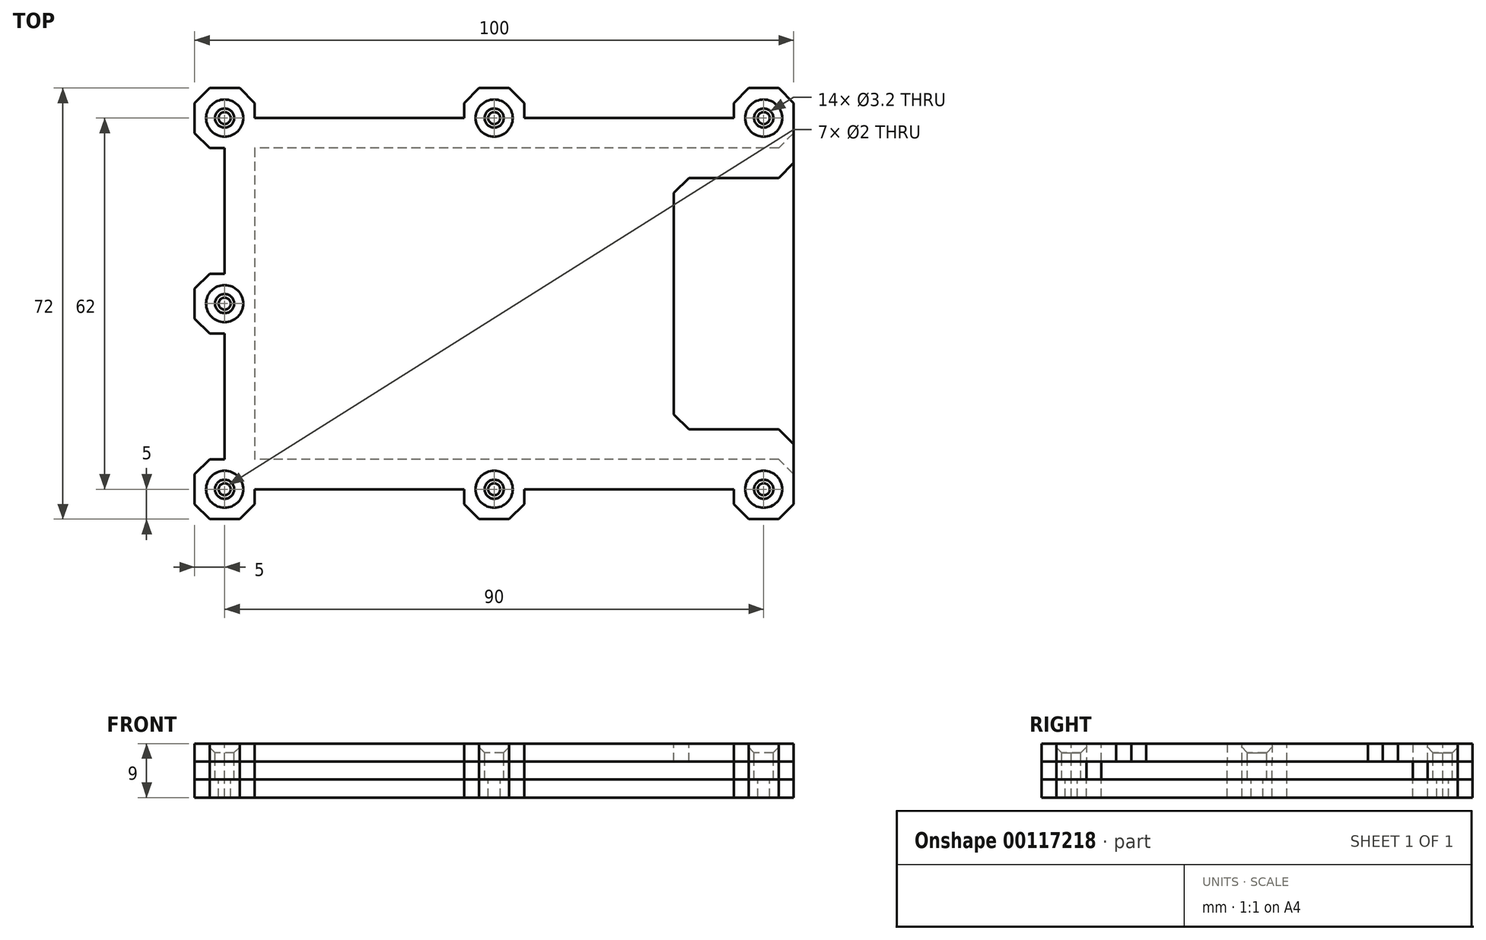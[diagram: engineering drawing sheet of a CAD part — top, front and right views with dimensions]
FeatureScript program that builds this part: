
annotation { "Feature Type Name" : "Feature", "Feature Type Description" : "" }
export const myFeature = defineFeature(function(context is Context, id is Id, definition is map)
    precondition{}
    {
        {
            var Q0;
            Q0=qCreatedBy(makeId("Top.planeOp"),FACE);
            var sketch = newSketch(context, id + "F0", { "sketchPlane" : qUnion([Q0])});
            skLineSegment(sketch, "E0.bottom", {"start": v(45, -26) * mm, "end": v(-37, -26) * mm});
            skLineSegment(sketch, "E0.top", {"start": v(45, 26) * mm, "end": v(-37, 26) * mm});
            skLineSegment(sketch, "E0.left", {"start": v(45, -36) * mm, "end": v(45, 36) * mm});
            skLineSegment(sketch, "E0.right", {"start": v(-45, -18) * mm, "end": v(-45, 18) * mm});
            skPoint(sketch, "E0.middle", {"position": v(0, 0) * mm});
            skPoint(sketch, "E1.visualSharp", {"position": v(-45, 26) * mm});
            skArc(sketch, "E1.filletArc", {"start": v(-37, 26) * mm, "mid": v(-42.66, 23.66) * mm, "end": v(-45, 18) * mm});
            skPoint(sketch, "E2.visualSharp", {"position": v(-45, -26) * mm});
            skArc(sketch, "E2.filletArc", {"start": v(-45, -18) * mm, "mid": v(-42.66, -23.66) * mm, "end": v(-37, -26) * mm});
            skLineSegment(sketch, "E3.bottom", {"start": v(45, -36) * mm, "end": v(35, -36) * mm});
            skLineSegment(sketch, "E3.right", {"start": v(-55, -36) * mm, "end": v(-55, -26) * mm});
            skLineSegment(sketch, "E4.top", {"start": v(-45, 31) * mm, "end": v(-10, 31) * mm});
            skLineSegment(sketch, "E4.left", {"start": v(-45, 36) * mm, "end": v(-45, 31) * mm});
            skLineSegment(sketch, "E4.right", {"start": v(-10, 36) * mm, "end": v(-10, 31) * mm});
            skLineSegment(sketch, "E5.top", {"start": v(0, 31) * mm, "end": v(35, 31) * mm});
            skLineSegment(sketch, "E5.left", {"start": v(0, 36) * mm, "end": v(0, 31) * mm});
            skLineSegment(sketch, "E5.right", {"start": v(35, 36) * mm, "end": v(35, 31) * mm});
            skLineSegment(sketch, "E6.bottom", {"start": v(0, -31) * mm, "end": v(35, -31) * mm});
            skLineSegment(sketch, "E6.left", {"start": v(0, -31) * mm, "end": v(0, -36) * mm});
            skLineSegment(sketch, "E6.right", {"start": v(35, -31) * mm, "end": v(35, -36) * mm});
            skLineSegment(sketch, "E7.bottom", {"start": v(-45, -31) * mm, "end": v(-10, -31) * mm});
            skLineSegment(sketch, "E7.left", {"start": v(-45, -31) * mm, "end": v(-45, -36) * mm});
            skLineSegment(sketch, "E7.right", {"start": v(-10, -31) * mm, "end": v(-10, -36) * mm});
            skLineSegment(sketch, "E8.trimOffspring", {"start": v(45, 36) * mm, "end": v(35, 36) * mm});
            skPoint(sketch, "E3.left.end.orphan", {"position": v(55, 36) * mm});
            skPoint(sketch, "E9.orphan", {"position": v(55, -36) * mm});
            skLineSegment(sketch, "E10.trimOffspring", {"start": v(-45, 36) * mm, "end": v(-55, 36) * mm});
            skLineSegment(sketch, "E11.trimOffspring", {"start": v(0, 36) * mm, "end": v(-10, 36) * mm});
            skLineSegment(sketch, "E12.trimOffspring", {"start": v(0, -36) * mm, "end": v(-10, -36) * mm});
            skLineSegment(sketch, "E13.trimOffspring", {"start": v(-45, -36) * mm, "end": v(-55, -36) * mm});
            skLineSegment(sketch, "E14.bottom", {"start": v(-55, 26) * mm, "end": v(-50, 26) * mm});
            skLineSegment(sketch, "E14.top", {"start": v(-55, 5) * mm, "end": v(-50, 5) * mm});
            skLineSegment(sketch, "E14.right", {"start": v(-50, 26) * mm, "end": v(-50, 5) * mm});
            skLineSegment(sketch, "E15.bottom", {"start": v(-55, -5) * mm, "end": v(-50, -5) * mm});
            skLineSegment(sketch, "E15.top", {"start": v(-55, -26) * mm, "end": v(-50, -26) * mm});
            skLineSegment(sketch, "E15.right", {"start": v(-50, -5) * mm, "end": v(-50, -26) * mm});
            skLineSegment(sketch, "E16.trimOffspring", {"start": v(-55, 26) * mm, "end": v(-55, 36) * mm});
            skLineSegment(sketch, "E17.trimOffspring", {"start": v(-55, -5) * mm, "end": v(-55, 5) * mm});
            skLineSegment(sketch, "E18", {"start": v(-45, 36) * mm, "end": v(-55, 26) * mm, "construction": true});
            skLineSegment(sketch, "E19", {"start": v(-10, 31) * mm, "end": v(0, 31) * mm, "construction": true});
            skLineSegment(sketch, "E20", {"start": v(35, 36) * mm, "end": v(45, 26) * mm, "construction": true});
            skLineSegment(sketch, "E21", {"start": v(45, -26) * mm, "end": v(35, -36) * mm, "construction": true});
            skLineSegment(sketch, "E22", {"start": v(0, -31) * mm, "end": v(-10, -31) * mm, "construction": true});
            skLineSegment(sketch, "E23", {"start": v(-45, -36) * mm, "end": v(-55, -26) * mm, "construction": true});
            skCircle(sketch, "E24", {"center": v(-50, 31) * mm, "radius": 1.6 * mm});
            skCircle(sketch, "E25", {"center": v(-5, 31) * mm, "radius": 1.6 * mm});
            skCircle(sketch, "E26", {"center": v(40, 31) * mm, "radius": 1.6 * mm});
            skCircle(sketch, "E27", {"center": v(40, -31) * mm, "radius": 1.6 * mm});
            skCircle(sketch, "E28", {"center": v(-5, -31) * mm, "radius": 1.6 * mm});
            skCircle(sketch, "E29", {"center": v(-50, -31) * mm, "radius": 1.6 * mm});
            skLineSegment(sketch, "E30", {"start": v(-50, 5) * mm, "end": v(-50, -5) * mm, "construction": true});
            skCircle(sketch, "E31", {"center": v(-50, 0) * mm, "radius": 1.6 * mm});
            skSolve(sketch);
        }
        {
            var Q0;
            {var subQ1=sQuery(id+"F0.wireOp",EDGE,"E0.bottom");Q0=makeQuery(id+"F0.imprint","IMPRINT",FACE,{"disambiguationData":[TD([[makeQuery(id+"F0.imprint","IMPRINT",EDGE,{"derivedFrom":subQ1}),-1.0]])]});}
            var Q1;
            {var subQ3=sQuery(id+"F0.wireOp",EDGE,"E0.bottom");Q1=makeQuery(id+"F0.imprint","IMPRINT",FACE,{"disambiguationData":[TD([[makeQuery(id+"F0.imprint","IMPRINT",EDGE,{"derivedFrom":subQ3}),1.0]])]});}
            extrude(context, id + "F1", {"entities" : qUnion([Q0, Q1]), "oppositeDirection" : true, "depth" : 3 * mm});
        }
        {
            var Q0;
            Q0=makeQuery(id+"F1.opExtrude","SWEPT_EDGE",EDGE,{"disambiguationData":[OSD([sQuery(id+"F0.wireOp",EDGE,"E0.left"),sQuery(id+"F0.wireOp",EDGE,"E3.bottom")])]});
            var Q1;
            Q1=makeQuery(id+"F1.opExtrude","SWEPT_EDGE",EDGE,{"disambiguationData":[OSD([sQuery(id+"F0.wireOp",EDGE,"E3.bottom"),sQuery(id+"F0.wireOp",EDGE,"E6.right")])]});
            var Q2;
            Q2=makeQuery(id+"F1.opExtrude","SWEPT_EDGE",EDGE,{"disambiguationData":[OSD([sQuery(id+"F0.wireOp",EDGE,"E6.left"),sQuery(id+"F0.wireOp",EDGE,"E12.trimOffspring")])]});
            var Q3;
            Q3=makeQuery(id+"F1.opExtrude","SWEPT_EDGE",EDGE,{"disambiguationData":[OSD([sQuery(id+"F0.wireOp",EDGE,"E7.right"),sQuery(id+"F0.wireOp",EDGE,"E12.trimOffspring")])]});
            var Q4;
            Q4=makeQuery(id+"F1.opExtrude","SWEPT_EDGE",EDGE,{"disambiguationData":[OSD([sQuery(id+"F0.wireOp",EDGE,"E7.left"),sQuery(id+"F0.wireOp",EDGE,"E13.trimOffspring")])]});
            var Q5;
            Q5=makeQuery(id+"F1.opExtrude","SWEPT_EDGE",EDGE,{"disambiguationData":[OSD([sQuery(id+"F0.wireOp",EDGE,"E3.right"),sQuery(id+"F0.wireOp",EDGE,"E13.trimOffspring")])]});
            var Q6;
            Q6=makeQuery(id+"F1.opExtrude","SWEPT_EDGE",EDGE,{"disambiguationData":[OSD([sQuery(id+"F0.wireOp",EDGE,"E15.bottom"),sQuery(id+"F0.wireOp",EDGE,"E17.trimOffspring")])]});
            var Q7;
            Q7=makeQuery(id+"F1.opExtrude","SWEPT_EDGE",EDGE,{"disambiguationData":[OSD([sQuery(id+"F0.wireOp",EDGE,"E14.bottom"),sQuery(id+"F0.wireOp",EDGE,"E16.trimOffspring")])]});
            var Q8;
            Q8=makeQuery(id+"F1.opExtrude","SWEPT_EDGE",EDGE,{"disambiguationData":[OSD([sQuery(id+"F0.wireOp",EDGE,"E3.right"),sQuery(id+"F0.wireOp",EDGE,"E15.top")])]});
            var Q9;
            Q9=makeQuery(id+"F1.opExtrude","SWEPT_EDGE",EDGE,{"disambiguationData":[OSD([sQuery(id+"F0.wireOp",EDGE,"E14.top"),sQuery(id+"F0.wireOp",EDGE,"E17.trimOffspring")])]});
            var Q10;
            Q10=makeQuery(id+"F1.opExtrude","SWEPT_EDGE",EDGE,{"disambiguationData":[OSD([sQuery(id+"F0.wireOp",EDGE,"E10.trimOffspring"),sQuery(id+"F0.wireOp",EDGE,"E16.trimOffspring")])]});
            var Q11;
            Q11=makeQuery(id+"F1.opExtrude","SWEPT_EDGE",EDGE,{"disambiguationData":[OSD([sQuery(id+"F0.wireOp",EDGE,"E4.left"),sQuery(id+"F0.wireOp",EDGE,"E10.trimOffspring")])]});
            var Q12;
            Q12=makeQuery(id+"F1.opExtrude","SWEPT_EDGE",EDGE,{"disambiguationData":[OSD([sQuery(id+"F0.wireOp",EDGE,"E4.right"),sQuery(id+"F0.wireOp",EDGE,"E11.trimOffspring")])]});
            var Q13;
            Q13=makeQuery(id+"F1.opExtrude","SWEPT_EDGE",EDGE,{"disambiguationData":[OSD([sQuery(id+"F0.wireOp",EDGE,"E5.left"),sQuery(id+"F0.wireOp",EDGE,"E11.trimOffspring")])]});
            var Q14;
            Q14=makeQuery(id+"F1.opExtrude","SWEPT_EDGE",EDGE,{"disambiguationData":[OSD([sQuery(id+"F0.wireOp",EDGE,"E5.right"),sQuery(id+"F0.wireOp",EDGE,"E8.trimOffspring")])]});
            var Q15;
            Q15=makeQuery(id+"F1.opExtrude","SWEPT_EDGE",EDGE,{"disambiguationData":[OSD([sQuery(id+"F0.wireOp",EDGE,"E0.left"),sQuery(id+"F0.wireOp",EDGE,"E8.trimOffspring")])]});
            chamfer(context, id + "F2", {"entities" : qUnion([Q0, Q1, Q2, Q3, Q4, Q5, Q6, Q7, Q8, Q9, Q10, Q11, Q12, Q13, Q14, Q15]), "width" : 2.5 * mm, "tangentPropagation" : true});
        }
        {
            var Q0;
            Q0=makeQuery(id+"F1.opExtrude","CAP_FACE",FACE,{"disambiguationData":[OSD([sQuery(id+"F0.wireOp",EDGE,"E0.left"),sQuery(id+"F0.wireOp",EDGE,"E3.bottom"),sQuery(id+"F0.wireOp",EDGE,"E3.right"),sQuery(id+"F0.wireOp",EDGE,"E4.top"),sQuery(id+"F0.wireOp",EDGE,"E4.left"),sQuery(id+"F0.wireOp",EDGE,"E4.right"),sQuery(id+"F0.wireOp",EDGE,"E5.top"),sQuery(id+"F0.wireOp",EDGE,"E5.left"),sQuery(id+"F0.wireOp",EDGE,"E5.right"),sQuery(id+"F0.wireOp",EDGE,"E6.bottom"),sQuery(id+"F0.wireOp",EDGE,"E6.left"),sQuery(id+"F0.wireOp",EDGE,"E6.right"),sQuery(id+"F0.wireOp",EDGE,"E7.bottom"),sQuery(id+"F0.wireOp",EDGE,"E7.left"),sQuery(id+"F0.wireOp",EDGE,"E7.right"),sQuery(id+"F0.wireOp",EDGE,"E8.trimOffspring"),sQuery(id+"F0.wireOp",EDGE,"E10.trimOffspring"),sQuery(id+"F0.wireOp",EDGE,"E11.trimOffspring"),sQuery(id+"F0.wireOp",EDGE,"E12.trimOffspring"),sQuery(id+"F0.wireOp",EDGE,"E13.trimOffspring"),sQuery(id+"F0.wireOp",EDGE,"E14.bottom"),sQuery(id+"F0.wireOp",EDGE,"E14.top"),sQuery(id+"F0.wireOp",EDGE,"E14.right"),sQuery(id+"F0.wireOp",EDGE,"E15.bottom"),sQuery(id+"F0.wireOp",EDGE,"E15.top"),sQuery(id+"F0.wireOp",EDGE,"E15.right"),sQuery(id+"F0.wireOp",EDGE,"E16.trimOffspring"),sQuery(id+"F0.wireOp",EDGE,"E17.trimOffspring"),sQuery(id+"F0.wireOp",EDGE,"E24"),sQuery(id+"F0.wireOp",EDGE,"E25"),sQuery(id+"F0.wireOp",EDGE,"E26"),sQuery(id+"F0.wireOp",EDGE,"E27"),sQuery(id+"F0.wireOp",EDGE,"E28"),sQuery(id+"F0.wireOp",EDGE,"E29"),sQuery(id+"F0.wireOp",EDGE,"E31")])],"isStart":false});
            var sketch = newSketch(context, id + "F3", { "sketchPlane" : qUnion([Q0])});
            skLineSegment(sketch, "E32", {"start": v(42.5, -36) * mm, "end": v(37.5, -36) * mm});
            skLineSegment(sketch, "E33", {"start": v(42.5, -36) * mm, "end": v(45, -33.5) * mm});
            skLineSegment(sketch, "E34", {"start": v(45, 33.5) * mm, "end": v(45, 26) * mm});
            skLineSegment(sketch, "E35", {"start": v(45, 33.5) * mm, "end": v(42.5, 36) * mm});
            skLineSegment(sketch, "E36", {"start": v(42.5, 36) * mm, "end": v(37.5, 36) * mm});
            skLineSegment(sketch, "E37", {"start": v(37.5, 36) * mm, "end": v(35, 33.5) * mm});
            skLineSegment(sketch, "E38", {"start": v(35, 31) * mm, "end": v(35, 33.5) * mm});
            skLineSegment(sketch, "E39", {"start": v(0, 31) * mm, "end": v(35, 31) * mm});
            skLineSegment(sketch, "E40", {"start": v(0, 31) * mm, "end": v(0, 33.5) * mm});
            skLineSegment(sketch, "E41", {"start": v(0, 33.5) * mm, "end": v(-2.5, 36) * mm});
            skLineSegment(sketch, "E42", {"start": v(-2.5, 36) * mm, "end": v(-7.5, 36) * mm});
            skLineSegment(sketch, "E43", {"start": v(-7.5, 36) * mm, "end": v(-10, 33.5) * mm});
            skLineSegment(sketch, "E44", {"start": v(-10, 31) * mm, "end": v(-10, 33.5) * mm});
            skLineSegment(sketch, "E45", {"start": v(-45, 31) * mm, "end": v(-10, 31) * mm});
            skLineSegment(sketch, "E46", {"start": v(-45, 31) * mm, "end": v(-45, 33.5) * mm});
            skLineSegment(sketch, "E47", {"start": v(-45, 33.5) * mm, "end": v(-47.5, 36) * mm});
            skLineSegment(sketch, "E48", {"start": v(-47.5, 36) * mm, "end": v(-52.5, 36) * mm});
            skLineSegment(sketch, "E49", {"start": v(-52.5, 36) * mm, "end": v(-55, 33.5) * mm});
            skLineSegment(sketch, "E50", {"start": v(-55, 33.5) * mm, "end": v(-55, 28.5) * mm});
            skLineSegment(sketch, "E51", {"start": v(-55, 28.5) * mm, "end": v(-52.5, 26) * mm});
            skLineSegment(sketch, "E52", {"start": v(-52.5, 26) * mm, "end": v(-50, 26) * mm});
            skLineSegment(sketch, "E53", {"start": v(-50, 5) * mm, "end": v(-50, 26) * mm});
            skLineSegment(sketch, "E54", {"start": v(-52.5, 5) * mm, "end": v(-50, 5) * mm});
            skLineSegment(sketch, "E55", {"start": v(-52.5, 5) * mm, "end": v(-55, 2.5) * mm});
            skLineSegment(sketch, "E56", {"start": v(-55, 2.5) * mm, "end": v(-55, -2.5) * mm});
            skLineSegment(sketch, "E57", {"start": v(-55, -2.5) * mm, "end": v(-52.5, -5) * mm});
            skLineSegment(sketch, "E58", {"start": v(-52.5, -5) * mm, "end": v(-50, -5) * mm});
            skLineSegment(sketch, "E59", {"start": v(-50, -26) * mm, "end": v(-50, -5) * mm});
            skLineSegment(sketch, "E60", {"start": v(-52.5, -26) * mm, "end": v(-50, -26) * mm});
            skLineSegment(sketch, "E61", {"start": v(-52.5, -26) * mm, "end": v(-55, -28.5) * mm});
            skLineSegment(sketch, "E62", {"start": v(-55, -28.5) * mm, "end": v(-55, -33.5) * mm});
            skLineSegment(sketch, "E63", {"start": v(-55, -33.5) * mm, "end": v(-52.5, -36) * mm});
            skLineSegment(sketch, "E64", {"start": v(-47.5, -36) * mm, "end": v(-52.5, -36) * mm});
            skLineSegment(sketch, "E65", {"start": v(-47.5, -36) * mm, "end": v(-45, -33.5) * mm});
            skLineSegment(sketch, "E66", {"start": v(-45, -33.5) * mm, "end": v(-45, -31) * mm});
            skLineSegment(sketch, "E67", {"start": v(-45, -31) * mm, "end": v(-10, -31) * mm});
            skLineSegment(sketch, "E68", {"start": v(-10, -33.5) * mm, "end": v(-10, -31) * mm});
            skLineSegment(sketch, "E69", {"start": v(-10, -33.5) * mm, "end": v(-7.5, -36) * mm});
            skLineSegment(sketch, "E70", {"start": v(-2.5, -36) * mm, "end": v(-7.5, -36) * mm});
            skLineSegment(sketch, "E71", {"start": v(-2.5, -36) * mm, "end": v(0, -33.5) * mm});
            skLineSegment(sketch, "E72", {"start": v(0, -33.5) * mm, "end": v(0, -31) * mm});
            skLineSegment(sketch, "E73", {"start": v(0, -31) * mm, "end": v(35, -31) * mm});
            skLineSegment(sketch, "E74", {"start": v(35, -33.5) * mm, "end": v(35, -31) * mm});
            skLineSegment(sketch, "E75", {"start": v(35, -33.5) * mm, "end": v(37.5, -36) * mm});
            skCircle(sketch, "E76", {"center": v(-50, 0) * mm, "radius": 1.6 * mm});
            skCircle(sketch, "E77", {"center": v(-50, 31) * mm, "radius": 1.6 * mm});
            skCircle(sketch, "E78", {"center": v(-5, 31) * mm, "radius": 1.6 * mm});
            skCircle(sketch, "E79", {"center": v(40, 31) * mm, "radius": 1.6 * mm});
            skCircle(sketch, "E80", {"center": v(40, -31) * mm, "radius": 1.6 * mm});
            skCircle(sketch, "E81", {"center": v(-5, -31) * mm, "radius": 1.6 * mm});
            skCircle(sketch, "E82", {"center": v(-50, -31) * mm, "radius": 1.6 * mm});
            skLineSegment(sketch, "E83", {"start": v(45, 33.5) * mm, "end": v(45, -33.5) * mm});
            skLineSegment(sketch, "E84.bottom", {"start": v(45, -26) * mm, "end": v(-45, -26) * mm});
            skLineSegment(sketch, "E84.top", {"start": v(45, 26) * mm, "end": v(-45, 26) * mm});
            skLineSegment(sketch, "E84.right", {"start": v(-45, -26) * mm, "end": v(-45, 26) * mm});
            skPoint(sketch, "E84.middle", {"position": v(0, 0) * mm});
            skLineSegment(sketch, "E85.trimOffspring", {"start": v(45, -26) * mm, "end": v(45, -33.5) * mm});
            skSolve(sketch);
        }
        {
            var Q0;
            Q0=makeQuery(id+"F3.imprint","IMPRINT",FACE,{"disambiguationData":[TD([[makeQuery(id+"F3.imprint","IMPRINT",EDGE,{"derivedFrom":sQuery(id+"F3.wireOp",EDGE,"E32")}),-1.0]])]});
            extrude(context, id + "F4", {"entities" : qUnion([Q0]), "depth" : 3 * mm});
        }
        {
            var Q0;
            Q0=makeQuery(id+"F4.opExtrude","CAP_FACE",FACE,{"disambiguationData":[OSD([sQuery(id+"F3.wireOp",EDGE,"E32"),sQuery(id+"F3.wireOp",EDGE,"E33"),sQuery(id+"F3.wireOp",EDGE,"E83"),sQuery(id+"F3.wireOp",EDGE,"E35"),sQuery(id+"F3.wireOp",EDGE,"E36"),sQuery(id+"F3.wireOp",EDGE,"E37"),sQuery(id+"F3.wireOp",EDGE,"E38"),sQuery(id+"F3.wireOp",EDGE,"E39"),sQuery(id+"F3.wireOp",EDGE,"E40"),sQuery(id+"F3.wireOp",EDGE,"E41"),sQuery(id+"F3.wireOp",EDGE,"E42"),sQuery(id+"F3.wireOp",EDGE,"E43"),sQuery(id+"F3.wireOp",EDGE,"E44"),sQuery(id+"F3.wireOp",EDGE,"E45"),sQuery(id+"F3.wireOp",EDGE,"E46"),sQuery(id+"F3.wireOp",EDGE,"E47"),sQuery(id+"F3.wireOp",EDGE,"E48"),sQuery(id+"F3.wireOp",EDGE,"E49"),sQuery(id+"F3.wireOp",EDGE,"E50"),sQuery(id+"F3.wireOp",EDGE,"E51"),sQuery(id+"F3.wireOp",EDGE,"E52"),sQuery(id+"F3.wireOp",EDGE,"E53"),sQuery(id+"F3.wireOp",EDGE,"E54"),sQuery(id+"F3.wireOp",EDGE,"E55"),sQuery(id+"F3.wireOp",EDGE,"E56"),sQuery(id+"F3.wireOp",EDGE,"E57"),sQuery(id+"F3.wireOp",EDGE,"E58"),sQuery(id+"F3.wireOp",EDGE,"E59"),sQuery(id+"F3.wireOp",EDGE,"E60"),sQuery(id+"F3.wireOp",EDGE,"E61"),sQuery(id+"F3.wireOp",EDGE,"E62"),sQuery(id+"F3.wireOp",EDGE,"E63"),sQuery(id+"F3.wireOp",EDGE,"E64"),sQuery(id+"F3.wireOp",EDGE,"E65"),sQuery(id+"F3.wireOp",EDGE,"E66"),sQuery(id+"F3.wireOp",EDGE,"E67"),sQuery(id+"F3.wireOp",EDGE,"E68"),sQuery(id+"F3.wireOp",EDGE,"E69"),sQuery(id+"F3.wireOp",EDGE,"E70"),sQuery(id+"F3.wireOp",EDGE,"E71"),sQuery(id+"F3.wireOp",EDGE,"E72"),sQuery(id+"F3.wireOp",EDGE,"E73"),sQuery(id+"F3.wireOp",EDGE,"E74"),sQuery(id+"F3.wireOp",EDGE,"E75"),sQuery(id+"F3.wireOp",EDGE,"E76"),sQuery(id+"F3.wireOp",EDGE,"E77"),sQuery(id+"F3.wireOp",EDGE,"E78"),sQuery(id+"F3.wireOp",EDGE,"E79"),sQuery(id+"F3.wireOp",EDGE,"E80"),sQuery(id+"F3.wireOp",EDGE,"E81"),sQuery(id+"F3.wireOp",EDGE,"E82"),sQuery(id+"F3.wireOp",EDGE,"E84.bottom"),sQuery(id+"F3.wireOp",EDGE,"E84.top"),sQuery(id+"F3.wireOp",EDGE,"E84.right"),sQuery(id+"F3.wireOp",EDGE,"E85.trimOffspring")])],"isStart":false});
            var sketch = newSketch(context, id + "F5", { "sketchPlane" : qUnion([Q0])});
            skLineSegment(sketch, "E86", {"start": v(45, -26) * mm, "end": v(45, -33.5) * mm});
            skLineSegment(sketch, "E87", {"start": v(42.5, -36) * mm, "end": v(45, -33.5) * mm});
            skLineSegment(sketch, "E88", {"start": v(42.5, -36) * mm, "end": v(37.5, -36) * mm});
            skLineSegment(sketch, "E89", {"start": v(35, -33.5) * mm, "end": v(37.5, -36) * mm});
            skLineSegment(sketch, "E90", {"start": v(35, -33.5) * mm, "end": v(35, -31) * mm});
            skLineSegment(sketch, "E91", {"start": v(0, -31) * mm, "end": v(35, -31) * mm});
            skLineSegment(sketch, "E92", {"start": v(0, -33.5) * mm, "end": v(0, -31) * mm});
            skLineSegment(sketch, "E93", {"start": v(-2.5, -36) * mm, "end": v(0, -33.5) * mm});
            skLineSegment(sketch, "E94", {"start": v(-2.5, -36) * mm, "end": v(-7.5, -36) * mm});
            skLineSegment(sketch, "E95", {"start": v(-10, -33.5) * mm, "end": v(-7.5, -36) * mm});
            skLineSegment(sketch, "E96", {"start": v(-10, -33.5) * mm, "end": v(-10, -31) * mm});
            skLineSegment(sketch, "E97", {"start": v(-45, -31) * mm, "end": v(-10, -31) * mm});
            skLineSegment(sketch, "E98", {"start": v(-45, -33.5) * mm, "end": v(-45, -31) * mm});
            skLineSegment(sketch, "E99", {"start": v(-47.5, -36) * mm, "end": v(-45, -33.5) * mm});
            skLineSegment(sketch, "E100", {"start": v(-47.5, -36) * mm, "end": v(-52.5, -36) * mm});
            skLineSegment(sketch, "E101", {"start": v(-55, -33.5) * mm, "end": v(-52.5, -36) * mm});
            skLineSegment(sketch, "E102", {"start": v(-55, -28.5) * mm, "end": v(-55, -33.5) * mm});
            skLineSegment(sketch, "E103", {"start": v(-52.5, -26) * mm, "end": v(-55, -28.5) * mm});
            skLineSegment(sketch, "E104", {"start": v(-52.5, -26) * mm, "end": v(-50, -26) * mm});
            skLineSegment(sketch, "E105", {"start": v(-50, -26) * mm, "end": v(-50, -5) * mm});
            skLineSegment(sketch, "E106", {"start": v(-52.5, -5) * mm, "end": v(-50, -5) * mm});
            skLineSegment(sketch, "E107", {"start": v(-55, -2.5) * mm, "end": v(-52.5, -5) * mm});
            skLineSegment(sketch, "E108", {"start": v(-55, 2.5) * mm, "end": v(-55, -2.5) * mm});
            skLineSegment(sketch, "E109", {"start": v(-52.5, 5) * mm, "end": v(-55, 2.5) * mm});
            skLineSegment(sketch, "E110", {"start": v(-52.5, 5) * mm, "end": v(-50, 5) * mm});
            skLineSegment(sketch, "E111", {"start": v(-50, 5) * mm, "end": v(-50, 26) * mm});
            skLineSegment(sketch, "E112", {"start": v(-52.5, 26) * mm, "end": v(-50, 26) * mm});
            skLineSegment(sketch, "E113", {"start": v(-55, 28.5) * mm, "end": v(-52.5, 26) * mm});
            skLineSegment(sketch, "E114", {"start": v(-55, 33.5) * mm, "end": v(-55, 28.5) * mm});
            skLineSegment(sketch, "E115", {"start": v(-52.5, 36) * mm, "end": v(-55, 33.5) * mm});
            skLineSegment(sketch, "E116", {"start": v(-47.5, 36) * mm, "end": v(-52.5, 36) * mm});
            skLineSegment(sketch, "E117", {"start": v(-45, 33.5) * mm, "end": v(-47.5, 36) * mm});
            skLineSegment(sketch, "E118", {"start": v(-45, 31) * mm, "end": v(-45, 33.5) * mm});
            skLineSegment(sketch, "E119", {"start": v(-45, 31) * mm, "end": v(-10, 31) * mm});
            skLineSegment(sketch, "E120", {"start": v(-10, 31) * mm, "end": v(-10, 33.5) * mm});
            skLineSegment(sketch, "E121", {"start": v(-7.5, 36) * mm, "end": v(-10, 33.5) * mm});
            skLineSegment(sketch, "E122", {"start": v(-2.5, 36) * mm, "end": v(-7.5, 36) * mm});
            skLineSegment(sketch, "E123", {"start": v(0, 33.5) * mm, "end": v(-2.5, 36) * mm});
            skLineSegment(sketch, "E124", {"start": v(0, 31) * mm, "end": v(0, 33.5) * mm});
            skLineSegment(sketch, "E125", {"start": v(0, 31) * mm, "end": v(35, 31) * mm});
            skLineSegment(sketch, "E126", {"start": v(35, 31) * mm, "end": v(35, 33.5) * mm});
            skLineSegment(sketch, "E127", {"start": v(37.5, 36) * mm, "end": v(35, 33.5) * mm});
            skLineSegment(sketch, "E128", {"start": v(42.5, 36) * mm, "end": v(37.5, 36) * mm});
            skLineSegment(sketch, "E129", {"start": v(45, 33.5) * mm, "end": v(42.5, 36) * mm});
            skLineSegment(sketch, "E130", {"start": v(45, 33.5) * mm, "end": v(45, 26) * mm});
            skCircle(sketch, "E131", {"center": v(-50, 31) * mm, "radius": 1 * mm});
            skCircle(sketch, "E132.0.1.0", {"center": v(-50, 0) * mm, "radius": 1 * mm});
            skCircle(sketch, "E132.0.2.0", {"center": v(-50, -31) * mm, "radius": 1 * mm});
            skCircle(sketch, "E132.1.0.0", {"center": v(-5, 31) * mm, "radius": 1 * mm});
            skCircle(sketch, "E132.1.2.0", {"center": v(-5, -31) * mm, "radius": 1 * mm});
            skCircle(sketch, "E132.2.0.0", {"center": v(40, 31) * mm, "radius": 1 * mm});
            skCircle(sketch, "E132.2.2.0", {"center": v(40, -31) * mm, "radius": 1 * mm});
            skLineSegment(sketch, "E132.direction1", {"start": v(-50, 31) * mm, "end": v(-5, 31) * mm, "construction": true});
            skLineSegment(sketch, "E132.direction2", {"start": v(-50, 31) * mm, "end": v(-50, 0) * mm, "construction": true});
            skLineSegment(sketch, "E133", {"start": v(45, 26) * mm, "end": v(45, -26) * mm});
            skSolve(sketch);
        }
        {
            var Q0;
            Q0 = qSketchRegion(id + "F5", true);
            extrude(context, id + "F6", {"entities" : qUnion([Q0]), "depth" : 3 * mm});
        }
        {
            var Q0;
            Q0=makeQuery(id+"F1.opExtrude","CAP_FACE",FACE,{"disambiguationData":[OSD([sQuery(id+"F0.wireOp",EDGE,"E0.left"),sQuery(id+"F0.wireOp",EDGE,"E3.bottom"),sQuery(id+"F0.wireOp",EDGE,"E3.right"),sQuery(id+"F0.wireOp",EDGE,"E4.top"),sQuery(id+"F0.wireOp",EDGE,"E4.left"),sQuery(id+"F0.wireOp",EDGE,"E4.right"),sQuery(id+"F0.wireOp",EDGE,"E5.top"),sQuery(id+"F0.wireOp",EDGE,"E5.left"),sQuery(id+"F0.wireOp",EDGE,"E5.right"),sQuery(id+"F0.wireOp",EDGE,"E6.bottom"),sQuery(id+"F0.wireOp",EDGE,"E6.left"),sQuery(id+"F0.wireOp",EDGE,"E6.right"),sQuery(id+"F0.wireOp",EDGE,"E7.bottom"),sQuery(id+"F0.wireOp",EDGE,"E7.left"),sQuery(id+"F0.wireOp",EDGE,"E7.right"),sQuery(id+"F0.wireOp",EDGE,"E8.trimOffspring"),sQuery(id+"F0.wireOp",EDGE,"E10.trimOffspring"),sQuery(id+"F0.wireOp",EDGE,"E11.trimOffspring"),sQuery(id+"F0.wireOp",EDGE,"E12.trimOffspring"),sQuery(id+"F0.wireOp",EDGE,"E13.trimOffspring"),sQuery(id+"F0.wireOp",EDGE,"E14.bottom"),sQuery(id+"F0.wireOp",EDGE,"E14.top"),sQuery(id+"F0.wireOp",EDGE,"E14.right"),sQuery(id+"F0.wireOp",EDGE,"E15.bottom"),sQuery(id+"F0.wireOp",EDGE,"E15.top"),sQuery(id+"F0.wireOp",EDGE,"E15.right"),sQuery(id+"F0.wireOp",EDGE,"E16.trimOffspring"),sQuery(id+"F0.wireOp",EDGE,"E17.trimOffspring"),sQuery(id+"F0.wireOp",EDGE,"E24"),sQuery(id+"F0.wireOp",EDGE,"E25"),sQuery(id+"F0.wireOp",EDGE,"E26"),sQuery(id+"F0.wireOp",EDGE,"E27"),sQuery(id+"F0.wireOp",EDGE,"E28"),sQuery(id+"F0.wireOp",EDGE,"E29"),sQuery(id+"F0.wireOp",EDGE,"E31")])],"isStart":true});
            var sketch = newSketch(context, id + "F7", { "sketchPlane" : qUnion([Q0])});
            skLineSegment(sketch, "E134.bottom", {"start": v(65, -21) * mm, "end": v(25, -21) * mm});
            skLineSegment(sketch, "E134.top", {"start": v(65, 21) * mm, "end": v(25, 21) * mm});
            skLineSegment(sketch, "E134.left", {"start": v(65, -21) * mm, "end": v(65, 21) * mm});
            skLineSegment(sketch, "E134.right", {"start": v(25, -21) * mm, "end": v(25, 21) * mm});
            skPoint(sketch, "E134.middle", {"position": v(45, 0) * mm});
            skLineSegment(sketch, "E135", {"start": v(-48.4, 0) * mm, "end": v(0, 0) * mm, "construction": true});
            skLineSegment(sketch, "E136.bottom", {"start": v(10, -21) * mm, "end": v(-10, -21) * mm});
            skLineSegment(sketch, "E136.top", {"start": v(10, 21) * mm, "end": v(-10, 21) * mm});
            skLineSegment(sketch, "E136.left", {"start": v(10, -21) * mm, "end": v(10, 21) * mm});
            skLineSegment(sketch, "E136.right", {"start": v(-10, -21) * mm, "end": v(-10, 21) * mm});
            skPoint(sketch, "E136.middle", {"position": v(0, 0) * mm});
            skLineSegment(sketch, "E137.bottom", {"start": v(-25, -21) * mm, "end": v(-45, -21) * mm});
            skLineSegment(sketch, "E137.top", {"start": v(-25, 21) * mm, "end": v(-45, 21) * mm});
            skLineSegment(sketch, "E137.left", {"start": v(-25, -21) * mm, "end": v(-25, 21) * mm});
            skLineSegment(sketch, "E137.right", {"start": v(-45, -21) * mm, "end": v(-45, 21) * mm});
            skPoint(sketch, "E137.middle", {"position": v(-35, 0) * mm});
            skSolve(sketch);
        }
        {
            var Q0;
            {var subQ0=sQuery(id+"F7.wireOp",EDGE,"E134.left");Q0=makeQuery(id+"F7.imprint","IMPRINT",FACE,{"disambiguationData":[TD([[makeQuery(id+"F7.imprint","IMPRINT",EDGE,{"derivedFrom":subQ0}),1.0]])]});}
            var Q1;
            {var subQ0=sQuery(id+"F7.wireOp",EDGE,"E134.right");Q1=makeQuery(id+"F7.imprint","IMPRINT",FACE,{"disambiguationData":[TD([[makeQuery(id+"F7.imprint","IMPRINT",EDGE,{"derivedFrom":subQ0}),-1.0]])]});}
            extrude(context, id + "F8", {"entities" : qUnion([Q0, Q1]), "operationType" : NewBodyOperationType.REMOVE, "oppositeDirection" : true, "depth" : 4 * mm});
        }
        {
            var Q0;
            Q0=makeQuery(id+"F8.boolean.opBoolean","COPY",EDGE,{"derivedFrom":makeQuery(id+"F8.opExtrude","SWEPT_EDGE",EDGE,{"disambiguationData":[OSD([sQuery(id+"F7.wireOp",EDGE,"E134.top"),sQuery(id+"F7.wireOp",EDGE,"E134.right")])]})});
            var Q1;
            Q1=makeQuery(id+"F8.boolean.opBoolean","INTERSECT",EDGE,{"derivedFrom":[makeQuery(id+"F1.opExtrude","SWEPT_FACE",FACE,{"disambiguationData":[OSD([sQuery(id+"F0.wireOp",EDGE,"E0.left")])]}),makeQuery(id+"F8.opExtrude","SWEPT_FACE",FACE,{"disambiguationData":[OSD([sQuery(id+"F7.wireOp",EDGE,"E134.top")])]})]});
            var Q2;
            Q2=makeQuery(id+"F8.boolean.opBoolean","INTERSECT",EDGE,{"derivedFrom":[makeQuery(id+"F1.opExtrude","SWEPT_FACE",FACE,{"disambiguationData":[OSD([sQuery(id+"F0.wireOp",EDGE,"E0.left")])]}),makeQuery(id+"F8.opExtrude","SWEPT_FACE",FACE,{"disambiguationData":[OSD([sQuery(id+"F7.wireOp",EDGE,"E134.bottom")])]})]});
            var Q3;
            Q3=makeQuery(id+"F8.boolean.opBoolean","COPY",EDGE,{"derivedFrom":makeQuery(id+"F8.opExtrude","SWEPT_EDGE",EDGE,{"disambiguationData":[OSD([sQuery(id+"F7.wireOp",EDGE,"E134.bottom"),sQuery(id+"F7.wireOp",EDGE,"E134.right")])]})});
            var Q4;
            Q4=makeQuery(id+"F4.opExtrude","SWEPT_EDGE",EDGE,{"disambiguationData":[OSD([sQuery(id+"F3.wireOp",EDGE,"E83"),sQuery(id+"F3.wireOp",EDGE,"E84.top")])]});
            var Q5;
            Q5=makeQuery(id+"F4.opExtrude","SWEPT_EDGE",EDGE,{"disambiguationData":[OSD([sQuery(id+"F3.wireOp",EDGE,"E83"),sQuery(id+"F3.wireOp",EDGE,"E84.bottom"),sQuery(id+"F3.wireOp",EDGE,"E85.trimOffspring")])]});
            chamfer(context, id + "F9", {"entities" : qUnion([Q0, Q1, Q2, Q3, Q4, Q5]), "width" : 2.5 * mm, "tangentPropagation" : true});
        }
        {
            var Q0;
            Q0=makeQuery(id+"F1.opExtrude","CAP_EDGE",EDGE,{"disambiguationData":[OSD([sQuery(id+"F0.wireOp",EDGE,"E26")])],"isStart":true});
            var Q1;
            Q1=makeQuery(id+"F1.opExtrude","CAP_EDGE",EDGE,{"disambiguationData":[OSD([sQuery(id+"F0.wireOp",EDGE,"E25")])],"isStart":true});
            var Q2;
            Q2=makeQuery(id+"F1.opExtrude","CAP_EDGE",EDGE,{"disambiguationData":[OSD([sQuery(id+"F0.wireOp",EDGE,"E24")])],"isStart":true});
            var Q3;
            Q3=makeQuery(id+"F1.opExtrude","CAP_EDGE",EDGE,{"disambiguationData":[OSD([sQuery(id+"F0.wireOp",EDGE,"E31")])],"isStart":true});
            var Q4;
            Q4=makeQuery(id+"F1.opExtrude","CAP_EDGE",EDGE,{"disambiguationData":[OSD([sQuery(id+"F0.wireOp",EDGE,"E29")])],"isStart":true});
            var Q5;
            Q5=makeQuery(id+"F1.opExtrude","CAP_EDGE",EDGE,{"disambiguationData":[OSD([sQuery(id+"F0.wireOp",EDGE,"E28")])],"isStart":true});
            var Q6;
            Q6=makeQuery(id+"F1.opExtrude","CAP_EDGE",EDGE,{"disambiguationData":[OSD([sQuery(id+"F0.wireOp",EDGE,"E27")])],"isStart":true});
            chamfer(context, id + "F10", {"entities" : qUnion([Q0, Q1, Q2, Q3, Q4, Q5, Q6]), "width" : 1.5 * mm, "tangentPropagation" : true});
        }
    });
